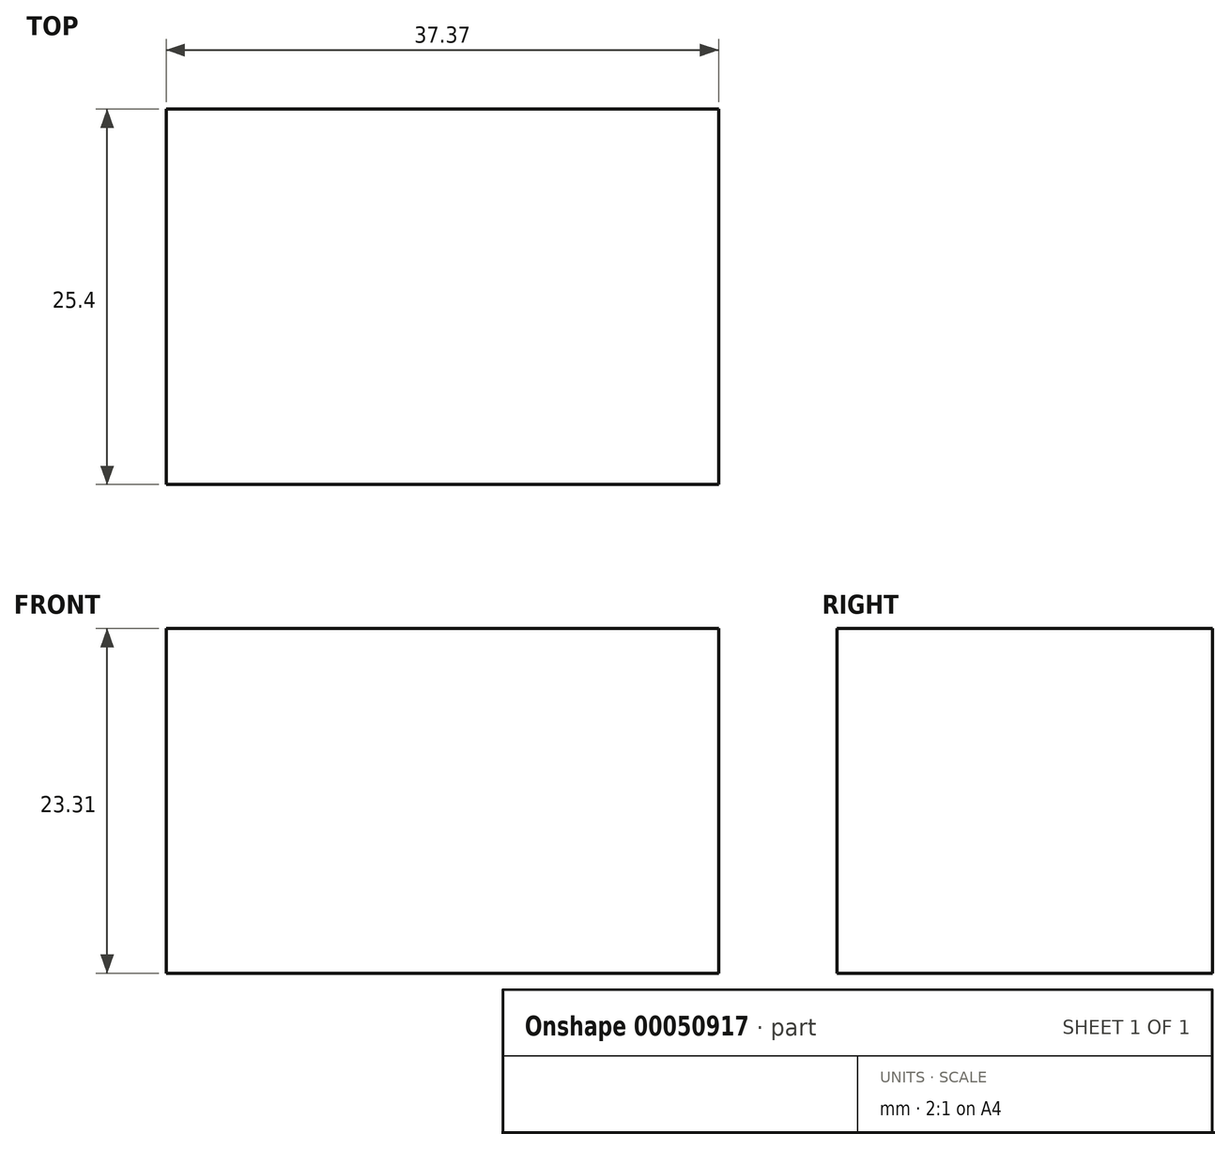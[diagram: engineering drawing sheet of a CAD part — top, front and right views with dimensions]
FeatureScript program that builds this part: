
annotation { "Feature Type Name" : "Feature", "Feature Type Description" : "" }
export const myFeature = defineFeature(function(context is Context, id is Id, definition is map)
    precondition{}
    {
        {
            var Q0;
            Q0=qCreatedBy(makeId("Front.planeOp"),FACE);
            var sketch = newSketch(context, id + "F0", { "sketchPlane" : qUnion([Q0])});
            skLineSegment(sketch, "E0.bottom", {"start": v(-57.53, 46.34) * mm, "end": v(-20.16, 46.34) * mm});
            skLineSegment(sketch, "E0.top", {"start": v(-57.53, 23.03) * mm, "end": v(-20.16, 23.03) * mm});
            skLineSegment(sketch, "E0.left", {"start": v(-57.53, 46.34) * mm, "end": v(-57.53, 23.03) * mm});
            skLineSegment(sketch, "E0.right", {"start": v(-20.16, 46.34) * mm, "end": v(-20.16, 23.03) * mm});
            skSolve(sketch);
        }
        {
            var Q0;
            Q0=makeQuery(id+"F0.imprint","IMPRINT",FACE,{"disambiguationData":[TD([[makeQuery(id+"F0.imprint","IMPRINT",EDGE,{"derivedFrom":sQuery(id+"F0.wireOp",EDGE,"E0.bottom")}),-1.0]])]});
            extrude(context, id + "F1", {"entities" : qUnion([Q0]), "depth" : 25.4 * mm});
        }
    });
